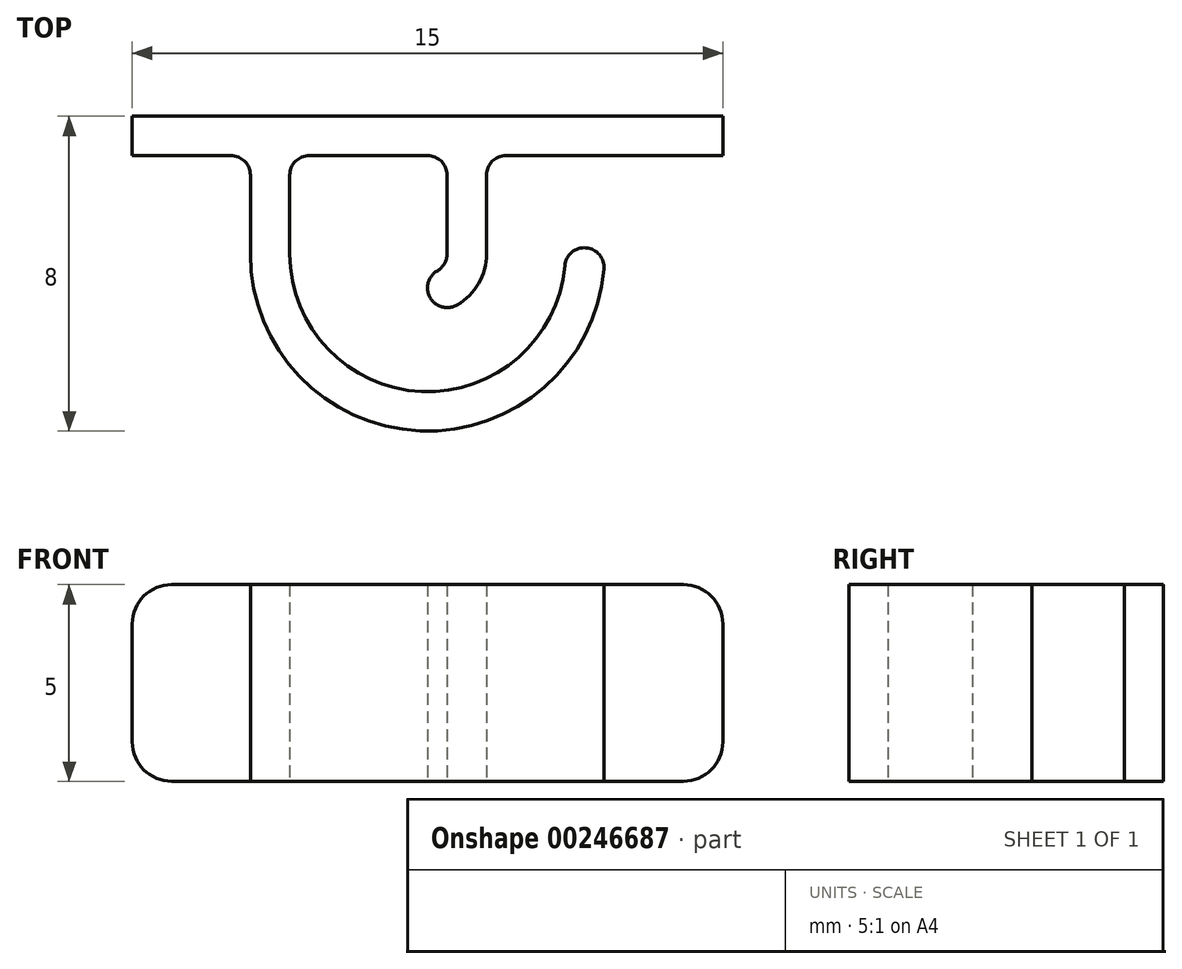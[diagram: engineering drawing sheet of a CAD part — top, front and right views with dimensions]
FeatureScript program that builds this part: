
annotation { "Feature Type Name" : "Feature", "Feature Type Description" : "" }
export const myFeature = defineFeature(function(context is Context, id is Id, definition is map)
    precondition{}
    {
        {
            var Q0;
            Q0=qCreatedBy(makeId("Top.planeOp"),FACE);
            var sketch = newSketch(context, id + "F0", { "sketchPlane" : qUnion([Q0])});
            skLineSegment(sketch, "E0.bottom", {"start": v(4.5, 0) * mm, "end": v(7.5, 0) * mm});
            skLineSegment(sketch, "E0.top", {"start": v(0, 1) * mm, "end": v(15, 1) * mm});
            skLineSegment(sketch, "E0.left", {"start": v(0, 0) * mm, "end": v(0, 1) * mm});
            skLineSegment(sketch, "E0.right", {"start": v(15, 0) * mm, "end": v(15, 1) * mm});
            skArc(sketch, "E1", {"start": v(3, -2.5) * mm, "mid": v(7.3, -7) * mm, "end": v(11.98, -2.89) * mm});
            skLineSegment(sketch, "E2", {"start": v(3, -2.5) * mm, "end": v(3, -0.5) * mm});
            skLineSegment(sketch, "E3", {"start": v(7.5, -2.5) * mm, "end": v(7.5, 0) * mm, "construction": true});
            skArc(sketch, "E4.0", {"start": v(4, -2.5) * mm, "mid": v(7.35, -6) * mm, "end": v(10.99, -2.8) * mm});
            skLineSegment(sketch, "E4.1", {"start": v(4, -2.5) * mm, "end": v(4, -0.5) * mm});
            skLineSegment(sketch, "E5", {"start": v(11.49, -2.34) * mm, "end": v(11.49, -2.34) * mm});
            skLineSegment(sketch, "E6", {"start": v(9, -0.5) * mm, "end": v(9, -2.5) * mm});
            skArc(sketch, "E7", {"start": v(9, -2.5) * mm, "mid": v(8.8, -3.25) * mm, "end": v(8.25, -3.8) * mm});
            skLineSegment(sketch, "E8", {"start": v(7.5, -3.36) * mm, "end": v(7.5, -3.36) * mm});
            skArc(sketch, "E9.0", {"start": v(8, -2.5) * mm, "mid": v(7.93, -2.75) * mm, "end": v(7.75, -2.93) * mm});
            skLineSegment(sketch, "E10", {"start": v(8, -2.5) * mm, "end": v(8, -0.5) * mm});
            skPoint(sketch, "E11.visualSharp", {"position": v(11, -2.34) * mm});
            skArc(sketch, "E11.filletArc", {"start": v(11.49, -2.34) * mm, "mid": v(11.15, -2.47) * mm, "end": v(10.99, -2.8) * mm});
            skPoint(sketch, "E12.visualSharp", {"position": v(12, -2.34) * mm});
            skArc(sketch, "E12.filletArc", {"start": v(11.98, -2.89) * mm, "mid": v(11.85, -2.5) * mm, "end": v(11.49, -2.34) * mm});
            skPoint(sketch, "E13.visualSharp", {"position": v(7.5, -3) * mm});
            skArc(sketch, "E13.filletArc", {"start": v(7.75, -2.93) * mm, "mid": v(7.57, -3.11) * mm, "end": v(7.5, -3.36) * mm});
            skPoint(sketch, "E14.visualSharp", {"position": v(7.5, -4) * mm});
            skArc(sketch, "E14.filletArc", {"start": v(7.5, -3.36) * mm, "mid": v(7.75, -3.8) * mm, "end": v(8.25, -3.8) * mm});
            skPoint(sketch, "E15.newPointB", {"position": v(0, 0) * mm});
            skArc(sketch, "E15.filletArc", {"start": v(4.5, 0) * mm, "mid": v(4.15, -0.15) * mm, "end": v(4, -0.5) * mm});
            skLineSegment(sketch, "E16", {"start": v(0, 0) * mm, "end": v(2.5, 0) * mm});
            skPoint(sketch, "E17.visualSharp", {"position": v(3, 0) * mm});
            skArc(sketch, "E17.filletArc", {"start": v(3, -0.5) * mm, "mid": v(2.85, -0.15) * mm, "end": v(2.5, 0) * mm});
            skPoint(sketch, "E18.newPointA", {"position": v(8, 0) * mm});
            skPoint(sketch, "E18.newPointB", {"position": v(15, 0) * mm});
            skArc(sketch, "E18.filletArc", {"start": v(8, -0.5) * mm, "mid": v(7.85, -0.15) * mm, "end": v(7.5, 0) * mm});
            skLineSegment(sketch, "E19", {"start": v(9.5, 0) * mm, "end": v(15, 0) * mm});
            skPoint(sketch, "E20.visualSharp", {"position": v(9, 0) * mm});
            skArc(sketch, "E20.filletArc", {"start": v(9.5, 0) * mm, "mid": v(9.14, -0.15) * mm, "end": v(9, -0.5) * mm});
            skSolve(sketch);
        }
        {
            var Q0;
            Q0 = qSketchRegion(id + "F0", true);
            extrude(context, id + "F1", {"entities" : qUnion([Q0]), "depth" : 5 * mm});
        }
        {
            var Q0;
            Q0=makeQuery(id+"F1.opExtrude","CAP_EDGE",EDGE,{"disambiguationData":[OSD([sQuery(id+"F0.wireOp",EDGE,"E0.right")])],"isStart":false});
            var Q1;
            Q1=makeQuery(id+"F1.opExtrude","CAP_EDGE",EDGE,{"disambiguationData":[OSD([sQuery(id+"F0.wireOp",EDGE,"E0.right")])],"isStart":true});
            var Q2;
            Q2=makeQuery(id+"F1.opExtrude","CAP_EDGE",EDGE,{"disambiguationData":[OSD([sQuery(id+"F0.wireOp",EDGE,"E0.left")])],"isStart":false});
            var Q3;
            Q3=makeQuery(id+"F1.opExtrude","CAP_EDGE",EDGE,{"disambiguationData":[OSD([sQuery(id+"F0.wireOp",EDGE,"E0.left")])],"isStart":true});
            fillet(context, id + "F2", {"entities" : qUnion([Q0, Q1, Q2, Q3]), "radius" : 1 * mm, "tangentPropagation" : true, "allowEdgeOverflow" : false});
        }
    });
